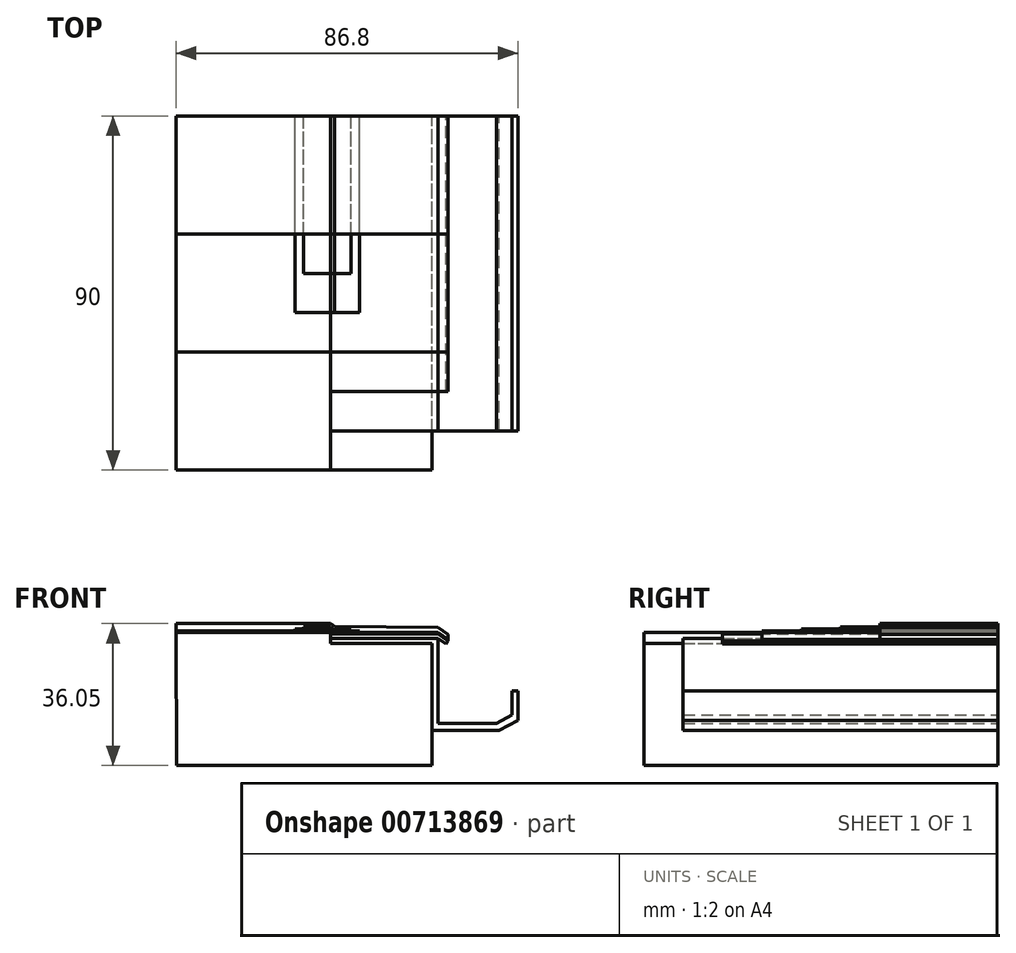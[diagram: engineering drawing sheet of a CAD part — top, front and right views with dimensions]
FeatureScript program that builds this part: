
annotation { "Feature Type Name" : "Feature", "Feature Type Description" : "" }
export const myFeature = defineFeature(function(context is Context, id is Id, definition is map)
    precondition{}
    {
        {
            var Q0;
            Q0=qCreatedBy(makeId("Front.planeOp"),FACE);
            var sketch = newSketch(context, id + "F0", { "sketchPlane" : qUnion([Q0])});
            skLineSegment(sketch, "E0", {"start": v(-75.03, 19.01) * mm, "end": v(-35.84, 19.01) * mm});
            skLineSegment(sketch, "E1", {"start": v(-35.84, 19.01) * mm, "end": v(-35.84, 16.28) * mm});
            skLineSegment(sketch, "E2", {"start": v(-35.84, 16.28) * mm, "end": v(-10, 16.28) * mm});
            skLineSegment(sketch, "E3", {"start": v(-10, 16.28) * mm, "end": v(-10, -14.78) * mm});
            skLineSegment(sketch, "E4", {"start": v(-10, -14.78) * mm, "end": v(-74.97, -14.78) * mm});
            skLineSegment(sketch, "E5", {"start": v(-74.97, -14.78) * mm, "end": v(-75.03, 19.01) * mm});
            skLineSegment(sketch, "E6", {"start": v(-10, -5.84) * mm, "end": v(7, -5.84) * mm});
            skLineSegment(sketch, "E7", {"start": v(7, -5.84) * mm, "end": v(11.77, -3.36) * mm});
            skLineSegment(sketch, "E8", {"start": v(11.77, -3.36) * mm, "end": v(11.77, 4.25) * mm});
            skLineSegment(sketch, "E9", {"start": v(-35.84, 17.55) * mm, "end": v(-8.56, 17.55) * mm});
            skLineSegment(sketch, "E10", {"start": v(-8.56, 17.55) * mm, "end": v(-8.56, -4.04) * mm});
            skLineSegment(sketch, "E11", {"start": v(-8.56, -4.04) * mm, "end": v(6.35, -4.04) * mm});
            skLineSegment(sketch, "E12", {"start": v(6.35, -4.04) * mm, "end": v(10.35, -1.92) * mm});
            skLineSegment(sketch, "E13", {"start": v(10.35, -1.92) * mm, "end": v(10.35, 4.2) * mm});
            skLineSegment(sketch, "E14", {"start": v(10.35, 4.2) * mm, "end": v(11.77, 4.25) * mm});
            skLineSegment(sketch, "E15", {"start": v(-8.56, 17.55) * mm, "end": v(-6.47, 16.15) * mm});
            skLineSegment(sketch, "E16", {"start": v(-6.47, 16.15) * mm, "end": v(-5.95, 16.94) * mm});
            skLineSegment(sketch, "E17", {"start": v(-5.95, 16.94) * mm, "end": v(-8.56, 18.69) * mm});
            skLineSegment(sketch, "E18", {"start": v(-8.56, 18.69) * mm, "end": v(-35.84, 18.69) * mm});
            skLineSegment(sketch, "E19", {"start": v(-75.03, 19.01) * mm, "end": v(-75.03, 19.4) * mm});
            skLineSegment(sketch, "E20", {"start": v(-75.03, 19.4) * mm, "end": v(-35.84, 19.4) * mm});
            skLineSegment(sketch, "E21", {"start": v(-35.84, 19.4) * mm, "end": v(-35.84, 19.01) * mm});
            skLineSegment(sketch, "E22", {"start": v(-35.84, 19.01) * mm, "end": v(-8.48, 19.01) * mm});
            skLineSegment(sketch, "E23", {"start": v(-8.48, 19.01) * mm, "end": v(-5.95, 17.32) * mm});
            skLineSegment(sketch, "E24", {"start": v(-5.95, 17.32) * mm, "end": v(-5.95, 16.94) * mm});
            skLineSegment(sketch, "E25", {"start": v(-44.83, 19.4) * mm, "end": v(-44.83, 19.98) * mm});
            skLineSegment(sketch, "E26", {"start": v(-44.83, 19.98) * mm, "end": v(-35.84, 19.98) * mm});
            skLineSegment(sketch, "E27", {"start": v(-35.84, 19.98) * mm, "end": v(-34.74, 19.4) * mm});
            skLineSegment(sketch, "E28", {"start": v(-34.74, 19.4) * mm, "end": v(-28.5, 19.4) * mm});
            skLineSegment(sketch, "E29", {"start": v(-28.5, 19.4) * mm, "end": v(-28.5, 19.01) * mm});
            skLineSegment(sketch, "E30", {"start": v(-42.7, 19.98) * mm, "end": v(-42.7, 20.43) * mm});
            skLineSegment(sketch, "E31", {"start": v(-42.7, 20.43) * mm, "end": v(-35.84, 20.43) * mm});
            skLineSegment(sketch, "E32", {"start": v(-35.84, 20.43) * mm, "end": v(-34.79, 19.72) * mm});
            skLineSegment(sketch, "E33", {"start": v(-34.79, 19.72) * mm, "end": v(-30.54, 19.72) * mm});
            skLineSegment(sketch, "E34", {"start": v(-30.54, 19.72) * mm, "end": v(-30.54, 19.4) * mm});
            skLineSegment(sketch, "E35", {"start": v(-75.03, 19.4) * mm, "end": v(-75.03, 21.27) * mm});
            skLineSegment(sketch, "E36", {"start": v(-75.03, 21.27) * mm, "end": v(-35.84, 21.27) * mm});
            skLineSegment(sketch, "E37", {"start": v(-35.84, 21.27) * mm, "end": v(-34.76, 20.54) * mm});
            skLineSegment(sketch, "E38", {"start": v(-34.76, 20.54) * mm, "end": v(-8.48, 20.27) * mm});
            skLineSegment(sketch, "E39", {"start": v(-8.48, 20.27) * mm, "end": v(-5.95, 18.56) * mm});
            skLineSegment(sketch, "E40", {"start": v(-5.95, 18.56) * mm, "end": v(-5.95, 17.32) * mm});
            skSolve(sketch);
        }
        {
            var Q0;
            {var subQ4=sQuery(id+"F0.wireOp",EDGE,"E0");Q0=makeQuery(id+"F0.imprint","IMPRINT",FACE,{"disambiguationData":[TD([[makeQuery(id+"F0.imprint","IMPRINT",EDGE,{"derivedFrom":subQ4}),-1.0]])]});}
            extrude(context, id + "F1", {"entities" : qUnion([Q0]), "depth" : 90 * mm});
        }
        {
            var Q0;
            {var subQ1=sQuery(id+"F0.wireOp",EDGE,"E2");Q0=makeQuery(id+"F0.imprint","IMPRINT",FACE,{"disambiguationData":[TD([[makeQuery(id+"F0.imprint","IMPRINT",EDGE,{"derivedFrom":subQ1}),1.0]])]});}
            extrude(context, id + "F2", {"entities" : qUnion([Q0]), "depth" : 80 * mm});
        }
        {
            var Q0;
            {var subQ0=sQuery(id+"F0.wireOp",EDGE,"E9");Q0=makeQuery(id+"F0.imprint","IMPRINT",FACE,{"disambiguationData":[TD([[makeQuery(id+"F0.imprint","IMPRINT",EDGE,{"derivedFrom":subQ0}),1.0]])]});}
            extrude(context, id + "F3", {"entities" : qUnion([Q0]), "depth" : 70 * mm});
        }
        {
            var Q0;
            Q0=makeQuery(id+"F0.imprint","IMPRINT",FACE,{"disambiguationData":[TD([[makeQuery(id+"F0.imprint","IMPRINT",EDGE,{"derivedFrom":sQuery(id+"F0.wireOp",EDGE,"E0")}),1.0]])]});
            extrude(context, id + "F4", {"entities" : qUnion([Q0]), "depth" : 60 * mm});
        }
        {
            var Q0;
            Q0=makeQuery(id+"F0.imprint","IMPRINT",FACE,{"disambiguationData":[TD([[makeQuery(id+"F0.imprint","IMPRINT",EDGE,{"derivedFrom":sQuery(id+"F0.wireOp",EDGE,"E17")}),-1.0]])]});
            extrude(context, id + "F5", {"entities" : qUnion([Q0]), "depth" : 60 * mm});
        }
        {
            var Q0;
            {var subQ1=sQuery(id+"F0.wireOp",EDGE,"E21");Q0=makeQuery(id+"F0.imprint","IMPRINT",FACE,{"disambiguationData":[TD([[makeQuery(id+"F0.imprint","IMPRINT",EDGE,{"derivedFrom":subQ1}),1.0]])]});}
            extrude(context, id + "F6", {"entities" : qUnion([Q0]), "depth" : 50 * mm});
        }
        {
            var Q0;
            {var subQ1=sQuery(id+"F0.wireOp",EDGE,"E27");Q0=makeQuery(id+"F0.imprint","IMPRINT",FACE,{"disambiguationData":[TD([[makeQuery(id+"F0.imprint","IMPRINT",EDGE,{"derivedFrom":subQ1}),1.0]])]});}
            extrude(context, id + "F7", {"entities" : qUnion([Q0]), "depth" : 40 * mm});
        }
        {
            var Q0;
            {var subQ8=sQuery(id+"F0.wireOp",EDGE,"E23");Q0=makeQuery(id+"F0.imprint","IMPRINT",FACE,{"disambiguationData":[TD([[makeQuery(id+"F0.imprint","IMPRINT",EDGE,{"derivedFrom":subQ8}),1.0]])]});}
            extrude(context, id + "F8", {"entities" : qUnion([Q0]), "depth" : 30 * mm});
        }
    });
